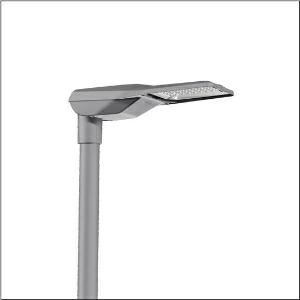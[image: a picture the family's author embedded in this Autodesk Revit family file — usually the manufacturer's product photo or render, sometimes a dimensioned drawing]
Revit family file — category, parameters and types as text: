
# Revit family: streetlight_sl_21_iq_mini___st1_0a_5xe2d41d08hb_6636
name_source: partatom
category: Lighting Fixtures
units: mm (PartAtom-declared; Revit-internal decimal feet)

## family parameters
Cut with Voids When Loaded = No
Host = Face
Light Source = No
Part Type = Normal
Room Calculation Point = No
Round Connector Dimension = Use Diameter
Shared = No

## types (1)
- --- (1 x LED, 9860 lm, 70.9 W, 4000K)
    Apparent Load = 71 VA
    CIE Flux Codes = 37 72 97 100 100
    Color Rendering = 70
    Color Temperature = 4000K
    Default Elevation = 1800 mm
    Description = Streetlight SL 21 iQ mini, mast luminaire, primary light control with lens, of PMMA, primary optical cover: cover, of toughened safety glass, transparent, light distribution: ST1.0a, light emission: direct distribution, primary light characteristic: asymmetric, installation type: post-top, side-entry, LED, High Power LED, rated luminous flux: 9.860lm, luminous efficacy: 139lm/W, light colour: 740, colour temperature: 4000K, control: Auto-Match, Temp-Guard, Lumen-Switch, Night-Set, Smart-Wire, Light-Fading, Desk-Remote (wireless, voltage-free reading and setting of iQ features in the workshop via application-optimized NFC function/RFID function), optimised constant luminous flux control (CLO 2.0), presetting dimming linear, mains connection: 220..240V, AC, 50/60Hz, start of lifetime: 71W, end of service life: 75W, reduction: 31W, luminaire housing, of diecast aluminium, powder-coated, Siteco® metallic grey (DB 702S), corrosivity category C5 mid according to DIN EN ISO 12944, please order mast flange separately, inclination adjustable: 0°, 5°, 10°, 15°, sealing non-destructively replaceable, multi-level sealing system, length: 628mm, width: 235mm, height: 110mm, mast flange for spigot size: 42mm (side-entry): 5XC10008XM4, 60/48mm (side-entry/post-top): 5XC10108XM2, 76/60mm (side-entry/post-top): 5XC10108XM1, protection rating (complete): IP66, insulation class (complete): insulation class II (safety insulation), certification: CE, ENEC, ENEC+, VDE, impact resistance: IK09, permissible operating ambient temperature for outdoor applications: -40..+50°C, standard-compliant lighting for roads and squares, packaging unit: 1 piece

Light Distribution: ST1.0a
    Height = 110 mm
    Lamp = 1 x LED
    Lamp Light Flux = 9860 lm
    Lamp Power = 70.9 W
    Lamp count = 1
    Length = 625 mm
    Luminous efficacy = 139 lm/W
    Manufacturer = Siteco
    ModVariant = No
    Model = 5XE2D41D08HB
    Number of Poles = 1
    OnlyDefault = Yes
    Power Factor = 1
    Product Name = Streetlight SL 21 iQ mini | ST1.0a
    Product group = mast luminaire | pylon top
    ProductGroupID = 6100
    Protection Class = Protection class II
    Protection Degree = IP 66
    RLX_Detail_Level = 1
    RLX_Emergency_Light_Flux = 0 lm
    RLX_Emergency_Type = 0
    RLX_Emergency_Type_DB = No
    RlxData = <blob elided: 91981 chars, md5=23d33b9e>
    Socket = socket
    Standby Power = 0 W
    System Light Flux = 9860 lm
    System Power = 71 W
    Type Comments = factory setting: luminous flux: 100 % | dim-lin: 254 | 711 mA
    Type Image = l_1003519.jpg
    URL = http://relux.com
    VarID = @adj_108271
    Voltage = 0 V
    Weight = 0.00 kg
    Width = 234 mm

## geometry (parser evidence)
native form markers: Blend x4, Sweep x12
no freeform markers — native parametric forms only
